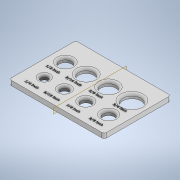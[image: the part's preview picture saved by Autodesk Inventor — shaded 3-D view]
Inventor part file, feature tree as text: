
AUTODESK INVENTOR PART (.ipt)
format: ipt  version: 2020.3 (Build 243373000, 373)  size: 1,513,472 bytes
history: native  units: in
note: dims shown in document units (in); Inventor stores cm internally (conversion verified against a paired STEP export)
features: extrude x3, sketch x3, fillet x2
ambient origin geometry x8: Origin, YZ Plane, XZ Plane, XY Plane, X Axis, Y Axis, Z Axis, Center Point
bodies: Solid1 (feature_tree)
feature tree (8):
  extrude  "Extrusion1"  Depth=3.5in
  extrude  "Extrusion3"  Depth=5.0in
  extrude  "textLabels"  TaperAngle=0.0deg  [1 undecoded]
  fillet  "Fillet1"  Radius=0.3454in
  fillet  "Fillet2"  Radius=1.6in
  sketch  "Sketch1"  dims[d0=0.25in d1=0.0in d3=3.5in]
  sketch  "Sketch4"  dims[d13=5.0in d16=1.0in]
  sketch  "Sketch7"  dims[d37=0.322in d38=0.0in d39=0.0in d45=0.3454in d46=1.6in d47=0.125in d48=0.0in d50=90.0deg d52=90.0deg d53=90.0deg d54=90.0deg d55=90.0deg d56=90.0deg d57=0.4772in d58=0.125in d59=0.125in]
note: 1 required parameter value undecoded (feature->parameter linkage not recoverable at this tier; creation-order binding heuristic only, values carry confidence <= 0.55)
